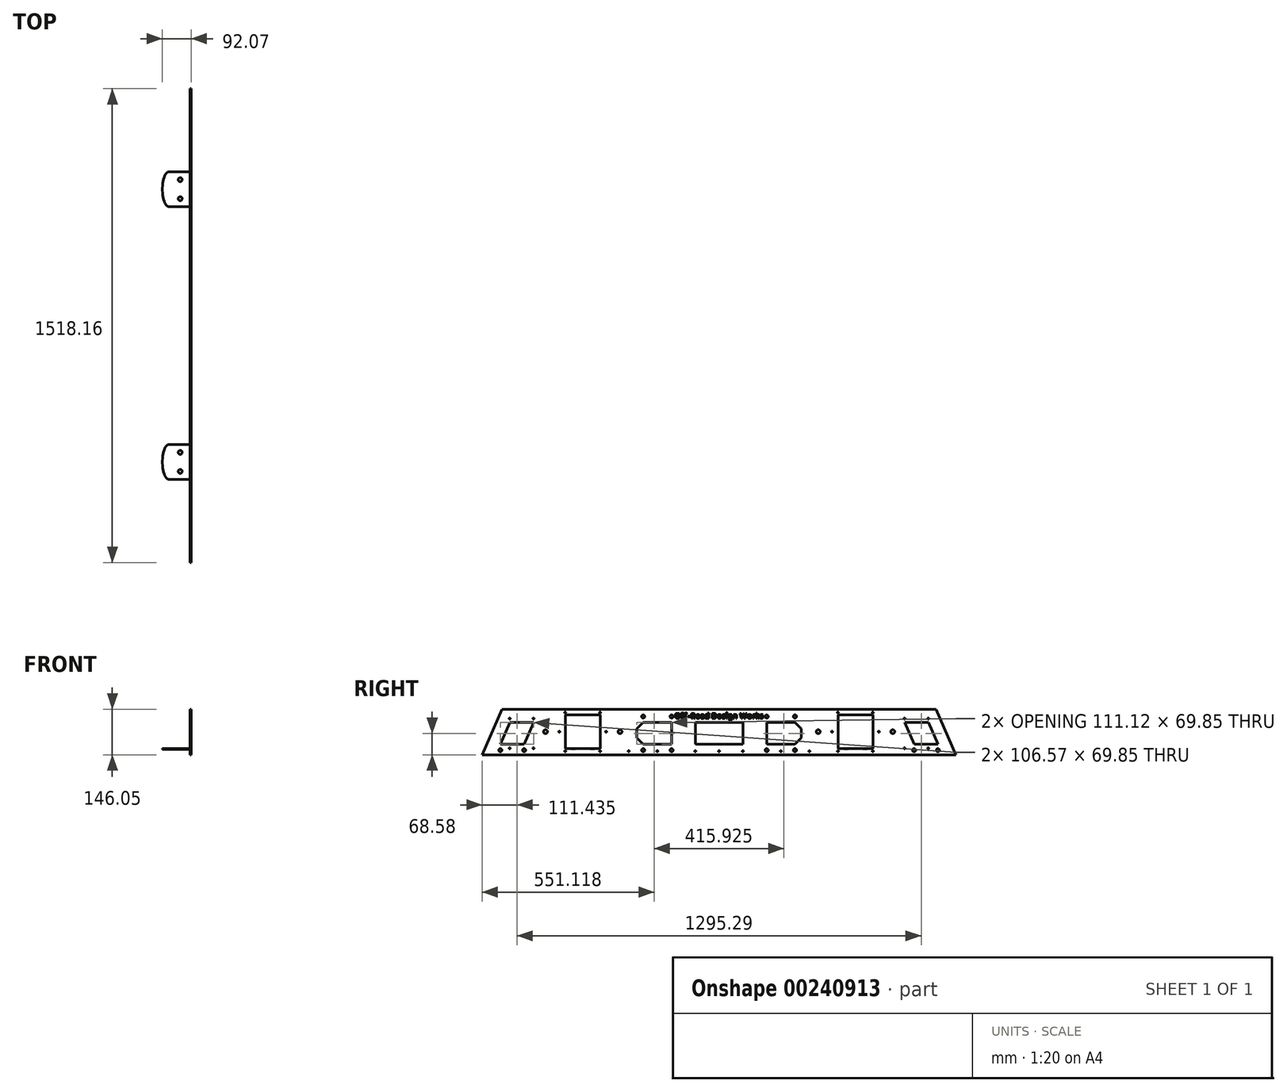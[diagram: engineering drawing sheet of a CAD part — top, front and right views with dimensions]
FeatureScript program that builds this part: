
annotation { "Feature Type Name" : "Feature", "Feature Type Description" : "" }
export const myFeature = defineFeature(function(context is Context, id is Id, definition is map)
    precondition{}
    {
        {
            var Q0;
            Q0=qCreatedBy(makeId("Right.planeOp"),FACE);
            var sketch = newSketch(context, id + "F0", { "sketchPlane" : qUnion([Q0])});
            skLineSegment(sketch, "E0", {"start": v(0, 0) * mm, "end": v(-759.08, 0) * mm});
            skLineSegment(sketch, "E1", {"start": v(-759.08, 0) * mm, "end": v(-695.58, 146.05) * mm});
            skLineSegment(sketch, "E2", {"start": v(-695.58, 146.05) * mm, "end": v(0, 146.05) * mm});
            skLineSegment(sketch, "E3", {"start": v(0, 0) * mm, "end": v(0, 460.36) * mm, "construction": true});
            skLineSegment(sketch, "E4.MirrorCS", {"start": v(695.58, 146.05) * mm, "end": v(0, 146.05) * mm});
            skLineSegment(sketch, "E5.MirrorCS", {"start": v(759.08, 0) * mm, "end": v(695.58, 146.05) * mm});
            skLineSegment(sketch, "E6.MirrorCS", {"start": v(0, 0) * mm, "end": v(759.08, 0) * mm});
            skSolve(sketch);
        }
        {
            var Q0;
            Q0=qSketchRegion(id+"F0",true);
            extrude(context, id + "F1", {"entities" : qUnion([Q0]), "oppositeDirection" : true, "depth" : 3.17 * mm});
        }
        {
            var Q0;
            Q0=makeQuery(id+"F1.opExtrude","CAP_FACE",FACE,{"disambiguationData":[OSD([sQuery(id+"F0.wireOp",EDGE,"E0"),sQuery(id+"F0.wireOp",EDGE,"E1"),sQuery(id+"F0.wireOp",EDGE,"E2"),sQuery(id+"F0.wireOp",EDGE,"E4.MirrorCS"),sQuery(id+"F0.wireOp",EDGE,"E5.MirrorCS"),sQuery(id+"F0.wireOp",EDGE,"E6.MirrorCS")])],"isStart":true});
            var sketch = newSketch(context, id + "F2", { "sketchPlane" : qUnion([Q0])});
            skLineSegment(sketch, "E7", {"start": v(0, 0) * mm, "end": v(0, 457.35) * mm, "construction": true});
            skLineSegment(sketch, "E8.bottom", {"start": v(-492.76, 127.5) * mm, "end": v(-381, 127.5) * mm});
            skLineSegment(sketch, "E8.top", {"start": v(-492.76, 20.32) * mm, "end": v(-381, 20.32) * mm});
            skLineSegment(sketch, "E8.left", {"start": v(-492.76, 127.5) * mm, "end": v(-492.76, 20.32) * mm});
            skLineSegment(sketch, "E8.right", {"start": v(-381, 127.5) * mm, "end": v(-381, 20.32) * mm});
            skLineSegment(sketch, "E9", {"start": v(-594.36, 103.5) * mm, "end": v(-670.56, 103.5) * mm});
            skLineSegment(sketch, "E10", {"start": v(-670.56, 103.5) * mm, "end": v(-700.93, 33.65) * mm});
            skLineSegment(sketch, "E11", {"start": v(-700.93, 33.65) * mm, "end": v(-624.73, 33.65) * mm});
            skLineSegment(sketch, "E12", {"start": v(-624.73, 33.65) * mm, "end": v(-594.36, 103.5) * mm});
            skArc(sketch, "E13.cCircle", {"start": v(-228.6, 103.5) * mm, "mid": v(-263.53, 68.58) * mm, "end": v(-228.6, 33.65) * mm, "construction": true});
            skLineSegment(sketch, "E13.0", {"start": v(-243.07, 103.5) * mm, "end": v(-214.13, 103.5) * mm});
            skLineSegment(sketch, "E13.4", {"start": v(-214.13, 33.65) * mm, "end": v(-243.07, 33.65) * mm});
            skLineSegment(sketch, "E13.5", {"start": v(-243.07, 33.65) * mm, "end": v(-263.53, 54.11) * mm});
            skLineSegment(sketch, "E13.6", {"start": v(-263.53, 54.11) * mm, "end": v(-263.53, 83.05) * mm});
            skLineSegment(sketch, "E13.7", {"start": v(-263.53, 83.05) * mm, "end": v(-243.07, 103.5) * mm});
            skPoint(sketch, "E13.0.midPoint", {"position": v(-228.6, 103.5) * mm});
            skLineSegment(sketch, "E14", {"start": v(-228.6, 33.65) * mm, "end": v(-152.4, 33.65) * mm});
            skLineSegment(sketch, "E15.MirrorCS", {"start": v(492.76, 127.5) * mm, "end": v(381, 127.5) * mm});
            skLineSegment(sketch, "E16.MirrorCS", {"start": v(492.76, 20.32) * mm, "end": v(381, 20.32) * mm});
            skLineSegment(sketch, "E17.MirrorCS", {"start": v(492.76, 127.5) * mm, "end": v(492.76, 20.32) * mm});
            skLineSegment(sketch, "E18.MirrorCS", {"start": v(381, 127.5) * mm, "end": v(381, 20.32) * mm});
            skLineSegment(sketch, "E19.MirrorCS", {"start": v(594.36, 103.5) * mm, "end": v(670.56, 103.5) * mm});
            skLineSegment(sketch, "E20.MirrorCS", {"start": v(670.56, 103.5) * mm, "end": v(700.93, 33.66) * mm});
            skLineSegment(sketch, "E21.MirrorCS", {"start": v(700.93, 33.65) * mm, "end": v(624.73, 33.65) * mm});
            skLineSegment(sketch, "E22.MirrorCS", {"start": v(624.73, 33.65) * mm, "end": v(594.36, 103.5) * mm});
            skLineSegment(sketch, "E23.MirrorCS", {"start": v(263.53, 54.11) * mm, "end": v(263.53, 83.05) * mm});
            skLineSegment(sketch, "E24.MirrorCS", {"start": v(263.53, 83.05) * mm, "end": v(243.07, 103.5) * mm});
            skArc(sketch, "E25.MirrorCS", {"start": v(228.6, 103.5) * mm, "mid": v(263.53, 68.58) * mm, "end": v(228.6, 33.65) * mm, "construction": true});
            skLineSegment(sketch, "E26.MirrorCS", {"start": v(243.07, 33.65) * mm, "end": v(263.53, 54.11) * mm});
            skLineSegment(sketch, "E27.MirrorCS", {"start": v(214.13, 33.65) * mm, "end": v(243.07, 33.65) * mm});
            skLineSegment(sketch, "E28.MirrorCS", {"start": v(243.07, 103.5) * mm, "end": v(214.13, 103.5) * mm});
            skLineSegment(sketch, "E29.MirrorCS", {"start": v(0, 103.5) * mm, "end": v(76.2, 103.5) * mm});
            skLineSegment(sketch, "E30.MirrorCS", {"start": v(228.6, 33.65) * mm, "end": v(152.4, 33.65) * mm});
            skLineSegment(sketch, "E31", {"start": v(-114.3, 103.5) * mm, "end": v(-114.3, -30.3) * mm, "construction": true});
            skLineSegment(sketch, "E32", {"start": v(-152.4, 103.5) * mm, "end": v(-152.4, 33.65) * mm});
            skLineSegment(sketch, "E33.MirrorCS", {"start": v(-76.2, 103.5) * mm, "end": v(-76.2, 33.65) * mm});
            skLineSegment(sketch, "E34.trimOffspring", {"start": v(-152.4, 103.5) * mm, "end": v(-228.6, 103.5) * mm});
            skPoint(sketch, "E35.start.orphan", {"position": v(0, 103.5) * mm});
            skLineSegment(sketch, "E36.trimOffspring", {"start": v(-76.2, 33.65) * mm, "end": v(0, 33.65) * mm});
            skLineSegment(sketch, "E37", {"start": v(-76.2, 103.5) * mm, "end": v(0, 103.5) * mm});
            skLineSegment(sketch, "E38", {"start": v(114.3, 103.5) * mm, "end": v(114.3, -63.26) * mm, "construction": true});
            skPoint(sketch, "E38.endSnap0", {"position": v(114.3, 103.5) * mm});
            skLineSegment(sketch, "E39", {"start": v(152.4, 103.5) * mm, "end": v(152.4, 33.65) * mm});
            skLineSegment(sketch, "E40.MirrorCS", {"start": v(76.2, 103.5) * mm, "end": v(76.2, 33.65) * mm});
            skLineSegment(sketch, "E41.trimOffspring", {"start": v(152.4, 103.5) * mm, "end": v(228.6, 103.5) * mm});
            skLineSegment(sketch, "E42.trimOffspring", {"start": v(76.2, 33.65) * mm, "end": v(0, 33.65) * mm});
            skSolve(sketch);
        }
        {
            var Q0;
            Q0=qSketchRegion(id+"F2",true);
            var Q1;
            Q1=makeQuery(id+"F1.opExtrude","CAP_FACE",FACE,{"disambiguationData":[OSD([sQuery(id+"F0.wireOp",EDGE,"E0"),sQuery(id+"F0.wireOp",EDGE,"E1"),sQuery(id+"F0.wireOp",EDGE,"E2"),sQuery(id+"F0.wireOp",EDGE,"E4.MirrorCS"),sQuery(id+"F0.wireOp",EDGE,"E5.MirrorCS"),sQuery(id+"F0.wireOp",EDGE,"E6.MirrorCS")])],"isStart":false});
            extrude(context, id + "F3", {"entities" : qUnion([Q0]), "operationType" : NewBodyOperationType.REMOVE, "endBound" : BoundingType.UP_TO_SURFACE, "oppositeDirection" : true, "endBoundEntityFace" : qUnion([Q1]), "depth" : 25.4 * mm});
        }
        {
            var Q0;
            Q0=makeQuery(id+"F1.opExtrude","CAP_FACE",FACE,{"disambiguationData":[OSD([sQuery(id+"F0.wireOp",EDGE,"E0"),sQuery(id+"F0.wireOp",EDGE,"E1"),sQuery(id+"F0.wireOp",EDGE,"E2"),sQuery(id+"F0.wireOp",EDGE,"E4.MirrorCS"),sQuery(id+"F0.wireOp",EDGE,"E5.MirrorCS"),sQuery(id+"F0.wireOp",EDGE,"E6.MirrorCS")])],"isStart":true});
            var sketch = newSketch(context, id + "F4", { "sketchPlane" : qUnion([Q0])});
            skCircle(sketch, "E43", {"center": v(-670.56, 116.2) * mm, "radius": 1.9 * mm});
            skCircle(sketch, "E44", {"center": v(-594.36, 116.2) * mm, "radius": 1.9 * mm});
            skCircle(sketch, "E45", {"center": v(-670.56, 20.95) * mm, "radius": 1.9 * mm});
            skCircle(sketch, "E46", {"center": v(-594.36, 20.95) * mm, "radius": 1.9 * mm});
            skCircle(sketch, "E47", {"center": v(-624.73, 14.6) * mm, "radius": 5.08 * mm});
            skCircle(sketch, "E48", {"center": v(-700.93, 14.6) * mm, "radius": 5.08 * mm});
            skCircle(sketch, "E49", {"center": v(-492.76, 135.13) * mm, "radius": 1.9 * mm});
            skCircle(sketch, "E50", {"center": v(-381, 135.13) * mm, "radius": 1.9 * mm});
            skLineSegment(sketch, "E51", {"start": v(-492.76, 73.91) * mm, "end": v(-416.14, 73.91) * mm, "construction": true});
            skCircle(sketch, "E52", {"center": v(-492.76, 11.43) * mm, "radius": 1.9 * mm});
            skCircle(sketch, "E53", {"center": v(-381, 11.43) * mm, "radius": 1.9 * mm});
            skCircle(sketch, "E54", {"center": v(-243.07, 14.6) * mm, "radius": 5.08 * mm});
            skCircle(sketch, "E55", {"center": v(-152.4, 14.6) * mm, "radius": 5.08 * mm});
            skLineSegment(sketch, "E56", {"start": v(-263.53, 68.58) * mm, "end": v(-277.88, 68.58) * mm, "construction": true});
            skCircle(sketch, "E57.MirrorC", {"center": v(-243.07, 122.56) * mm, "radius": 5.08 * mm});
            skCircle(sketch, "E58.MirrorC", {"center": v(-152.4, 122.56) * mm, "radius": 5.08 * mm});
            skLineSegment(sketch, "E59", {"start": v(0, 0) * mm, "end": v(0, -131.47) * mm, "construction": true});
            skCircle(sketch, "E60.MirrorC", {"center": v(152.4, 122.56) * mm, "radius": 5.08 * mm});
            skCircle(sketch, "E61.MirrorC", {"center": v(243.07, 122.56) * mm, "radius": 5.08 * mm});
            skCircle(sketch, "E62.MirrorC", {"center": v(243.07, 14.6) * mm, "radius": 5.08 * mm});
            skCircle(sketch, "E63.MirrorC", {"center": v(152.4, 14.6) * mm, "radius": 5.08 * mm});
            skCircle(sketch, "E64.MirrorC", {"center": v(381, 11.43) * mm, "radius": 1.9 * mm});
            skCircle(sketch, "E65.MirrorC", {"center": v(492.76, 11.43) * mm, "radius": 1.9 * mm});
            skCircle(sketch, "E66.MirrorC", {"center": v(492.76, 135.13) * mm, "radius": 1.9 * mm});
            skCircle(sketch, "E67.MirrorC", {"center": v(381, 135.13) * mm, "radius": 1.9 * mm});
            skCircle(sketch, "E68.MirrorC", {"center": v(594.36, 116.2) * mm, "radius": 1.9 * mm});
            skCircle(sketch, "E69.MirrorC", {"center": v(670.56, 116.2) * mm, "radius": 1.9 * mm});
            skCircle(sketch, "E70.MirrorC", {"center": v(670.56, 20.95) * mm, "radius": 1.9 * mm});
            skCircle(sketch, "E71.MirrorC", {"center": v(594.36, 20.95) * mm, "radius": 1.9 * mm});
            skCircle(sketch, "E72.MirrorC", {"center": v(624.73, 14.6) * mm, "radius": 5.08 * mm});
            skCircle(sketch, "E73.MirrorC", {"center": v(700.93, 14.6) * mm, "radius": 5.08 * mm});
            skCircle(sketch, "E74", {"center": v(-361.95, 73.91) * mm, "radius": 1.9 * mm});
            skPoint(sketch, "E74.centerSnap0", {"position": v(-381, 73.91) * mm});
            skCircle(sketch, "E75", {"center": v(-511.81, 73.91) * mm, "radius": 1.9 * mm});
            skCircle(sketch, "E76.MirrorC", {"center": v(361.95, 73.91) * mm, "radius": 1.9 * mm});
            skCircle(sketch, "E77.MirrorC", {"center": v(511.81, 73.91) * mm, "radius": 1.9 * mm});
            skCircle(sketch, "E78", {"center": v(-197.73, 11.43) * mm, "radius": 1.9 * mm});
            skPoint(sketch, "E78.centerSnap0", {"position": v(-197.73, 33.66) * mm});
            skCircle(sketch, "E79", {"center": v(-289.37, 11.43) * mm, "radius": 1.9 * mm});
            skCircle(sketch, "E80.MirrorC", {"center": v(197.73, 11.43) * mm, "radius": 1.9 * mm});
            skCircle(sketch, "E81.MirrorC", {"center": v(289.37, 11.43) * mm, "radius": 1.9 * mm});
            skCircle(sketch, "E82", {"center": v(-76.2, 11.43) * mm, "radius": 1.9 * mm});
            skCircle(sketch, "E83", {"center": v(0, 11.43) * mm, "radius": 1.9 * mm});
            skPoint(sketch, "E83.centerSnap0", {"position": v(0, 33.66) * mm});
            skCircle(sketch, "E84", {"center": v(76.2, 11.43) * mm, "radius": 1.9 * mm});
            skCircle(sketch, "E85", {"center": v(-317.5, 73.91) * mm, "radius": 6.35 * mm});
            skCircle(sketch, "E86", {"center": v(-556.26, 73.91) * mm, "radius": 6.35 * mm});
            skCircle(sketch, "E87.MirrorC", {"center": v(317.5, 73.91) * mm, "radius": 6.35 * mm});
            skCircle(sketch, "E88.MirrorC", {"center": v(556.26, 73.91) * mm, "radius": 6.35 * mm});
            skSolve(sketch);
        }
        {
            var Q0;
            Q0=qSketchRegion(id+"F4",true);
            var Q1;
            Q1=makeQuery(id+"F1.opExtrude","CAP_FACE",FACE,{"disambiguationData":[OSD([sQuery(id+"F0.wireOp",EDGE,"E0"),sQuery(id+"F0.wireOp",EDGE,"E1"),sQuery(id+"F0.wireOp",EDGE,"E2"),sQuery(id+"F0.wireOp",EDGE,"E4.MirrorCS"),sQuery(id+"F0.wireOp",EDGE,"E5.MirrorCS"),sQuery(id+"F0.wireOp",EDGE,"E6.MirrorCS")])],"isStart":false});
            extrude(context, id + "F5", {"entities" : qUnion([Q0]), "operationType" : NewBodyOperationType.REMOVE, "endBound" : BoundingType.UP_TO_SURFACE, "oppositeDirection" : true, "endBoundEntityFace" : qUnion([Q1]), "depth" : 25.4 * mm});
        }
        {
            var Q0;
            Q0=makeQuery(id+"F1.opExtrude","CAP_FACE",FACE,{"disambiguationData":[OSD([sQuery(id+"F0.wireOp",EDGE,"E0"),sQuery(id+"F0.wireOp",EDGE,"E1"),sQuery(id+"F0.wireOp",EDGE,"E2"),sQuery(id+"F0.wireOp",EDGE,"E4.MirrorCS"),sQuery(id+"F0.wireOp",EDGE,"E5.MirrorCS"),sQuery(id+"F0.wireOp",EDGE,"E6.MirrorCS")])],"isStart":true});
            var sketch = newSketch(context, id + "F6", { "sketchPlane" : qUnion([Q0])});
            skText(sketch, "E89", { "text": "Off-Road Design Works", "fontName": "AllertaStencil-Regular.ttf"});
            skLineSegment(sketch, "E90", {"start": v(0, 0) * mm, "end": v(0, -60.67) * mm, "construction": true});
            skLineSegment(sketch, "E91", {"start": v(0, 116.2) * mm, "end": v(0, 0) * mm, "construction": true});
            const initialGuessF6  = {"E89": [-0.14224, 0.1162, 1, 0, 0.01718]};
            skSetInitialGuess(sketch, initialGuessF6);
            skSolve(sketch);
        }
        {
            var Q0;
            Q0=qSketchRegion(id+"F6",true);
            var Q1;
            Q1=makeQuery(id+"F1.opExtrude","CAP_FACE",FACE,{"disambiguationData":[OSD([sQuery(id+"F0.wireOp",EDGE,"E0"),sQuery(id+"F0.wireOp",EDGE,"E1"),sQuery(id+"F0.wireOp",EDGE,"E2"),sQuery(id+"F0.wireOp",EDGE,"E4.MirrorCS"),sQuery(id+"F0.wireOp",EDGE,"E5.MirrorCS"),sQuery(id+"F0.wireOp",EDGE,"E6.MirrorCS")])],"isStart":false});
            extrude(context, id + "F7", {"entities" : qUnion([Q0]), "operationType" : NewBodyOperationType.REMOVE, "endBound" : BoundingType.UP_TO_SURFACE, "oppositeDirection" : true, "endBoundEntityFace" : qUnion([Q1]), "depth" : 25.4 * mm});
        }
        {
            var Q0;
            Q0=makeQuery(id+"F3.boolean.opBoolean","COPY",FACE,{"derivedFrom":makeQuery(id+"F3.opExtrude","SWEPT_FACE",FACE,{"disambiguationData":[OSD([sQuery(id+"F2.wireOp",EDGE,"E8.top")])]})});
            var sketch = newSketch(context, id + "F8", { "sketchPlane" : qUnion([Q0])});
            skLineSegment(sketch, "E92", {"start": v(-3.18, -436.88) * mm, "end": v(-45.3, -436.88) * mm, "construction": true});
            skLineSegment(sketch, "E93", {"start": v(-3.18, -492.76) * mm, "end": v(-71.76, -492.76) * mm});
            skLineSegment(sketch, "E94.MirrorCS", {"start": v(-3.18, -381) * mm, "end": v(-71.76, -381) * mm});
            skEllipticalArc(sketch, "E95", {});
            skLineSegment(sketch, "E96", {"start": v(-3.18, -492.76) * mm, "end": v(-3.18, -381) * mm});
            skCircle(sketch, "E97", {"center": v(-34.93, -467.36) * mm, "radius": 6.35 * mm});
            skCircle(sketch, "E98.MirrorC", {"center": v(-34.93, -406.4) * mm, "radius": 6.35 * mm});
            skLineSegment(sketch, "E99", {"start": v(0, 0) * mm, "end": v(-238.43, 0) * mm, "construction": true});
            skLineSegment(sketch, "E100.MirrorCS", {"start": v(-3.18, 381) * mm, "end": v(-71.76, 381) * mm});
            skEllipticalArc(sketch, "E101.MirrorCS", {});
            skCircle(sketch, "E102.MirrorC", {"center": v(-34.93, 406.4) * mm, "radius": 6.35 * mm});
            skCircle(sketch, "E103.MirrorC", {"center": v(-34.93, 467.36) * mm, "radius": 6.35 * mm});
            skLineSegment(sketch, "E104.MirrorCS", {"start": v(-3.18, 492.76) * mm, "end": v(-71.76, 492.76) * mm});
            skLineSegment(sketch, "E105.MirrorCS", {"start": v(-3.18, 492.76) * mm, "end": v(-3.18, 381) * mm});
            const initialGuessF8  = {"E95": [-0.071755, -0.43688, 0, -1, 0.05588, 0.02032, 3.141592653589793, 0], "E101.MirrorCS": [-0.071755, 0.43688, 0, 1, 0.05588, 0.02032, 0, 3.141592653589793]};
            skSetInitialGuess(sketch, initialGuessF8);
            skSolve(sketch);
        }
        {
            var Q0;
            Q0=qSketchRegion(id+"F8",true);
            extrude(context, id + "F9", {"entities" : qUnion([Q0]), "operationType" : NewBodyOperationType.ADD, "oppositeDirection" : true, "depth" : 3.17 * mm});
        }
    });
